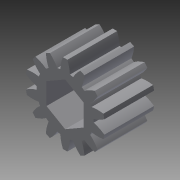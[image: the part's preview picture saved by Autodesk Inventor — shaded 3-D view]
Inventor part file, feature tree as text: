
AUTODESK INVENTOR PART (.ipt)
format: ipt  version: 2013 (Build 170138000, 138)  size: 164,352 bytes
history: native  units: in
note: dims shown in document units (in); Inventor stores cm internally (conversion verified against a paired STEP export)
features: other x2, extrude x2, sketch x2, imported_body x1
ambient origin geometry x8: Origin, YZ Plane, XZ Plane, XY Plane, X Axis, Y Axis, Z Axis, Center Point
feature tree (7):
  other  "Toughbox_d09"
  other  "Toughbox_d091"
  extrude  "Extrusion1"  Depth=0.5in TaperAngle=0.0deg
  extrude  "Extrusion2"  [1 undecoded]
  imported_body  "Base1"
  sketch  "Sketch1"  dims[d0=0.375in d1=0.5in d2=0.0in]
  sketch  "Sketch2"  dims[d3=0.5in d4=0.0in]
note: 1 required parameter value undecoded (feature->parameter linkage not recoverable at this tier; creation-order binding heuristic only, values carry confidence <= 0.55)
